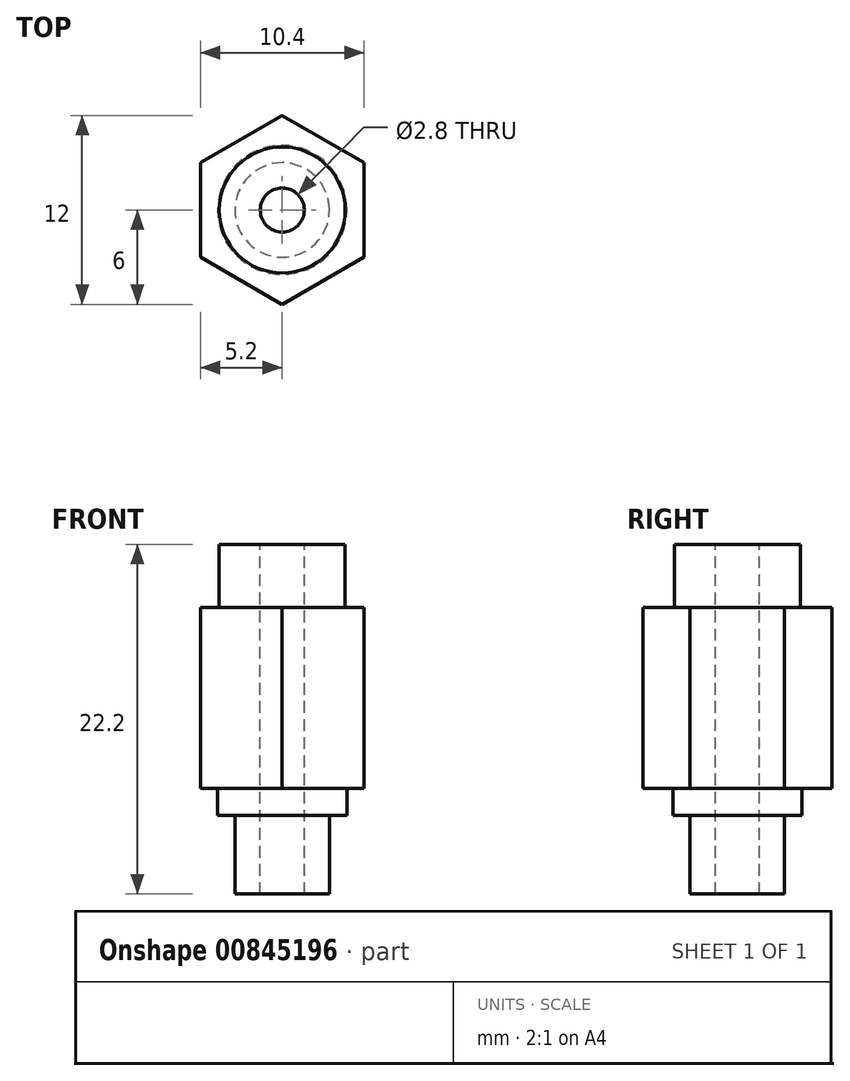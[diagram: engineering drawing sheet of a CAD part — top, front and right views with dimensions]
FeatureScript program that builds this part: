
annotation { "Feature Type Name" : "Feature", "Feature Type Description" : "" }
export const myFeature = defineFeature(function(context is Context, id is Id, definition is map)
    precondition{}
    {
        {
            var Q0;
            Q0=qCreatedBy(makeId("Top.planeOp"),FACE);
            var sketch = newSketch(context, id + "F0", { "sketchPlane" : qUnion([Q0])});
            skCircle(sketch, "E0", {"center": v(0, 0) * mm, "radius": 6 * mm});
            skCircle(sketch, "E1", {"center": v(0, 0) * mm, "radius": 4.1 * mm});
            skCircle(sketch, "E2.cCircle", {"center": v(0, 0) * mm, "radius": 6 * mm, "construction": true});
            skLineSegment(sketch, "E2.0", {"start": v(0, 6) * mm, "end": v(5.2, 3) * mm});
            skLineSegment(sketch, "E2.1", {"start": v(5.2, 3) * mm, "end": v(5.2, -3) * mm});
            skLineSegment(sketch, "E2.2", {"start": v(5.2, -3) * mm, "end": v(0, -6) * mm});
            skLineSegment(sketch, "E2.3", {"start": v(0, -6) * mm, "end": v(-5.2, -3) * mm});
            skLineSegment(sketch, "E2.4", {"start": v(-5.2, -3) * mm, "end": v(-5.2, 3) * mm});
            skLineSegment(sketch, "E2.5", {"start": v(-5.2, 3) * mm, "end": v(0, 6) * mm});
            skCircle(sketch, "E3", {"center": v(0, 0) * mm, "radius": 1.4 * mm});
            skSolve(sketch);
        }
        {
            var Q0;
            Q0=makeQuery(id+"F0.imprint","IMPRINT",FACE,{"disambiguationData":[TD([[makeQuery(id+"F0.imprint","IMPRINT",EDGE,{"derivedFrom":sQuery(id+"F0.wireOp",EDGE,"E1")}),1.0]])]});
            extrude(context, id + "F1", {"entities" : qUnion([Q0]), "oppositeDirection" : true, "depth" : 1.7 * mm, "offsetDistance" : 25 * mm});
        }
        {
            var Q0;
            Q0=makeQuery(id+"F1.opExtrude","CAP_FACE",FACE,{"disambiguationData":[OSD([sQuery(id+"F0.wireOp",EDGE,"E1")])],"isStart":false});
            var sketch = newSketch(context, id + "F2", { "sketchPlane" : qUnion([Q0])});
            skCircle(sketch, "E4", {"center": v(0, 0) * mm, "radius": 3 * mm});
            skSolve(sketch);
        }
        {
            var Q0;
            Q0=makeQuery(id+"F2.imprint","IMPRINT",FACE,{"disambiguationData":[TD([[makeQuery(id+"F2.imprint","IMPRINT",EDGE,{"derivedFrom":sQuery(id+"F2.wireOp",EDGE,"E4")}),1.0]])]});
            extrude(context, id + "F3", {"entities" : qUnion([Q0]), "operationType" : NewBodyOperationType.ADD, "depth" : 5 * mm, "offsetDistance" : 25 * mm});
        }
        {
            var Q0;
            Q0=makeQuery(id+"F0.imprint","IMPRINT",FACE,{"disambiguationData":[TD([[makeQuery(id+"F0.imprint","IMPRINT",EDGE,{"derivedFrom":sQuery(id+"F0.wireOp",EDGE,"E1")}),1.0]])]});
            var Q1;
            Q1=makeQuery(id+"F0.imprint","IMPRINT",FACE,{"disambiguationData":[TD([[makeQuery(id+"F0.imprint","IMPRINT",EDGE,{"derivedFrom":sQuery(id+"F0.wireOp",EDGE,"E1")}),-1.0]])]});
            extrude(context, id + "F4", {"entities" : qUnion([Q0, Q1]), "operationType" : NewBodyOperationType.ADD, "depth" : 11.5 * mm, "offsetDistance" : 25 * mm});
        }
        {
            var Q0;
            Q0=makeQuery(id+"F4.opExtrude","CAP_FACE",FACE,{"disambiguationData":[OSD([sQuery(id+"F0.wireOp",EDGE,"E2.0"),sQuery(id+"F0.wireOp",EDGE,"E2.1"),sQuery(id+"F0.wireOp",EDGE,"E2.2"),sQuery(id+"F0.wireOp",EDGE,"E2.3"),sQuery(id+"F0.wireOp",EDGE,"E2.4"),sQuery(id+"F0.wireOp",EDGE,"E2.5")])],"isStart":false});
            var sketch = newSketch(context, id + "F5", { "sketchPlane" : qUnion([Q0])});
            skCircle(sketch, "E5", {"center": v(0, 0) * mm, "radius": 4 * mm});
            skSolve(sketch);
        }
        {
            var Q0;
            Q0=makeQuery(id+"F5.imprint","IMPRINT",FACE,{"disambiguationData":[TD([[makeQuery(id+"F5.imprint","IMPRINT",EDGE,{"derivedFrom":sQuery(id+"F5.wireOp",EDGE,"E5")}),1.0]])]});
            extrude(context, id + "F6", {"entities" : qUnion([Q0]), "operationType" : NewBodyOperationType.ADD, "depth" : 4 * mm, "offsetDistance" : 25 * mm});
        }
    });
